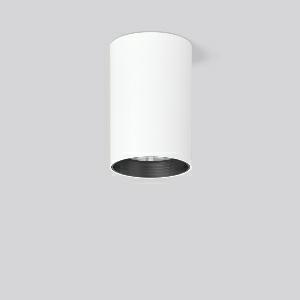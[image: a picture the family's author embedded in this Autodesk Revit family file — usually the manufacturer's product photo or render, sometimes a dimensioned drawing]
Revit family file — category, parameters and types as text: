
# Revit family: heledon_maxi_a_931227_002_76_4a27
name_source: partatom
category: Lighting Fixtures
units: mm (PartAtom-declared; Revit-internal decimal feet)

## family parameters
Cut with Voids When Loaded = No
Host = Face
Light Source = No
Part Type = Normal
Room Calculation Point = No
Round Connector Dimension = Use Diameter
Shared = No

## types (1)
- HELEDON maxi A (1 x LED Modul 930, 3650 lm, 3000)
    Apparent Load = 35 VA
    Approval mark = CE
    CIE Flux Codes = 97 100 100 100 100
    Color Rendering = 90
    Color Temperature = 3000
    Default Elevation = 1800 mm
    Description = Series: HELEDON maxi
Cylindrical surface-mounted downlight. Housing: die-cast aluminium, powder-coated. Internal ceiling frame polycarbonate with bayonet mounting. Black plastic ring and recessed LED to prevent glare from the side. Optical assembly with lens made of plastic (polycarbonate) for the best homogeneous light distribution - can be changed without tools. Best colour rendering index Ra>90. Suitable for Ceiling mounting. Easy installation with a separate ceiling frame with bayonet mounting and plug connection. Driver integrated. Connected via plug-in connector. High quality converter without flickering and stroboscopic effect. The following accessories can be mounted without use of tools: interchangeable lenses, decorative glasses, honeycomb louvre, clear and frosted diffusers, white interchangeable plastic ring. 
Colour: traffic white, matt (RAL 9016)
Diameter: 123 mm
Height: 183 mm
Lamp: LED
Socket: without socket
Colour temperature: 3000K
Colour rendering index (CRI): 92
System power: 35 W
Rated luminous flux: 3650 lm
Luminous efficiency: 104 lm/W
Control gear: Converter, dimmable, DALI
Protection class: I
Type of protection: IP 20
    Height = 183 mm
    Lamp = 1 x LED Modul 930
    Lamp Light Flux = 3650 lm
    Lamp count = 1
    Length = 123 mm
    Lifetime = 50000 h
    Luminous efficacy = 104 lm/W
    Manufacturer = RZB
    ModVariant = No
    Model = 931227.002.76
    Mounting Place = Ceiling
    Mounting Type = Surface mounted
    Number of Poles = 1
    OnlyDefault = Yes
    Power Factor = 1
    Product Name = HELEDON maxi A
    Product group = Surface mounted downlights
    ProductGroupID = 302
    Protection Class = Protection class I
    Protection Degree = IP 20
    RLX_Detail_Level = 1
    RLX_Emergency_Light_Flux = 0 lm
    RLX_Emergency_Type = 0
    RLX_Emergency_Type_DB = No
    RlxData = <blob elided: 96145 chars, md5=33d27f3d>
    Socket = socket
    Standby Power = 0 W
    System Light Flux = 3650 lm
    System Power = 35 W
    Type Comments = Product without accessories
    Type Image = 931193.002.jpg
    URL = http://relux.com
    VarID = ---
    Voltage = 230 V
    Voltage Range = 220-240 V
    Weight = 0.00 kg
    Width = 0 mm  [stored 0 ft]

note: [stored X ft] marks values corroborated as IEEE doubles in the binary element streams (Revit-internal decimal feet)

## geometry (parser evidence)
native form markers: Blend x4, Sweep x8
no freeform markers — native parametric forms only
